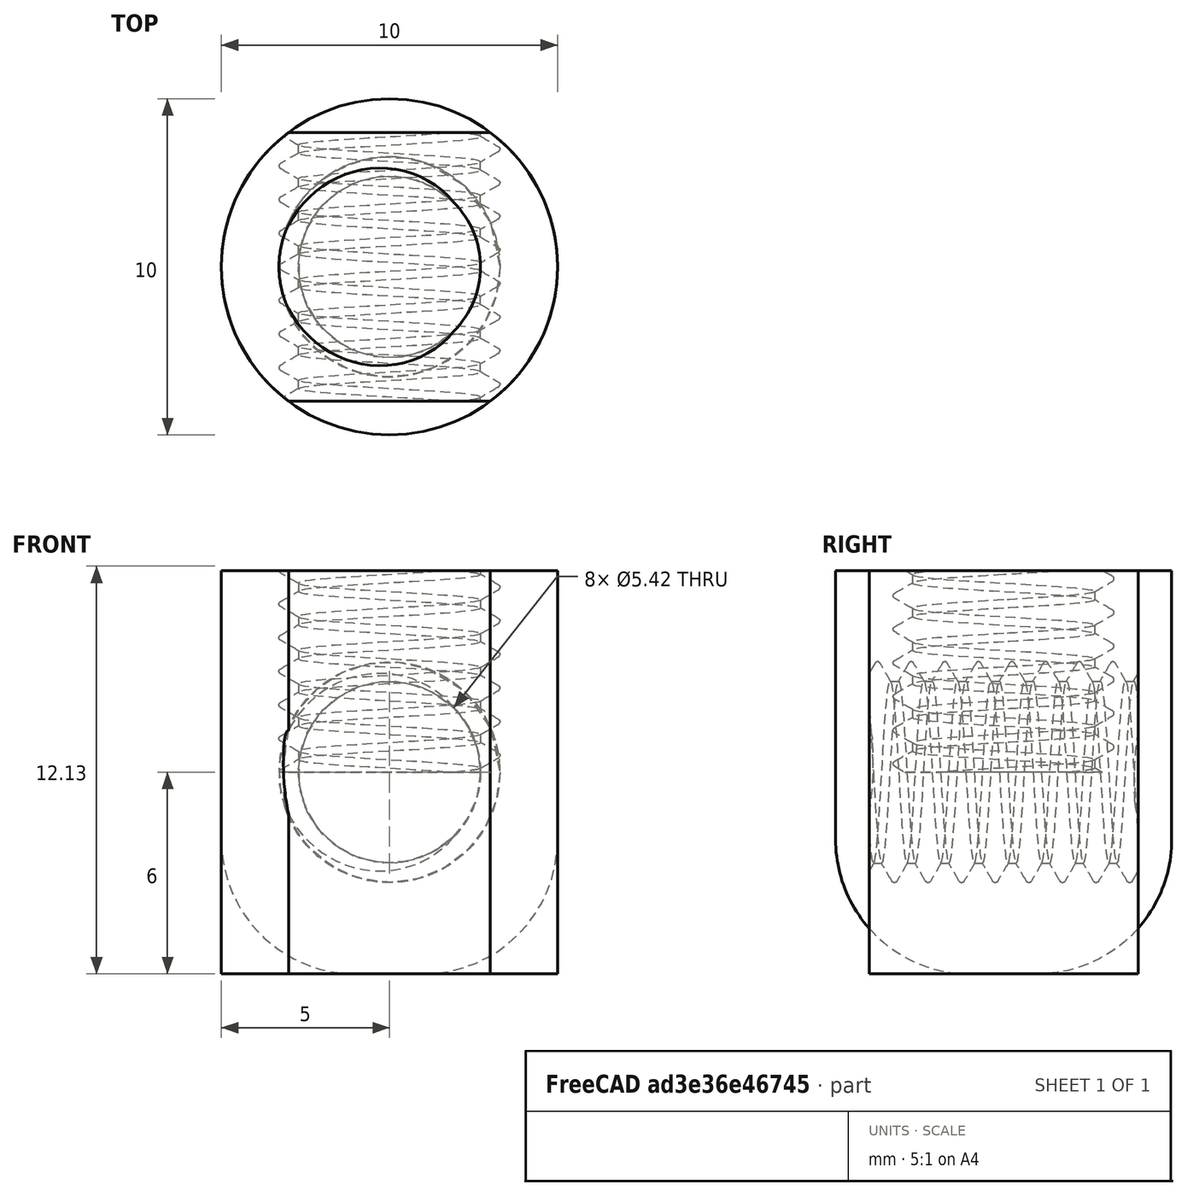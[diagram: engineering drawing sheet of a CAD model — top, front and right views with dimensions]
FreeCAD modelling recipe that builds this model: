
FCSTD DOCUMENT  (FreeCAD 0.21R33771 (Git))
Label: parts
License: All rights reserved
LicenseURL: https://en.wikipedia.org/wiki/All_rights_reserved
objects: Part::Cylinder×2, Part::FeaturePython×2, Part::Cut×2, Part::Box×1, Part::MultiCommon×1, Part::Fillet×1
note: 9 computed .brp shape members not serialized (recipe doc carries the construction recipe); baked Part::Feature solids carry a one-line shape summary decoded from their .brp

FEATURE [Part::Cylinder] Cylinder
  Angle = 360
  AttacherType = Attacher::AttachEngine3D
  FirstAngle = 0
  Height = 12
  Radius = 5
  SecondAngle = 0
FEATURE [Part::Box] Box  label="Cube"
  AttacherType = Attacher::AttachEngine3D
  Height = 12
  Length = 10
  Placement = pos=(-5,-4,0) rot=(0,0,1;0rad)
  Width = 8
FEATURE [Part::MultiCommon] Common
  Shapes = -> [Cylinder,Box]
FEATURE [Part::FeaturePython] ScrewTap  label="6.5x20-ScrewTap001"  # Fasteners workbench fastener (typed FeaturePython)
  Placement = pos=(0,-9,6) rot=(1,0,0;1.5708rad)
  diameter = 29
  diameterCustom = 6.5
  invert = false
  leftHanded = false
  length = 20
  matchOuter = false
  offset = 0
  pitchCustom = 1
  thread = true
  type = 2
FEATURE [Part::Cut] Cut  label="barrelnut_m6_threaded"
  Base = -> Common
  Tool = -> ScrewTap
FEATURE [Part::Cylinder] Cylinder001
  Angle = 360
  AttacherType = Attacher::AttachEngine3D
  FirstAngle = 0
  Height = 12
  Radius = 5
  SecondAngle = 0
FEATURE [Part::FeaturePython] ScrewTap001  label="6.5x20-ScrewTap"  # Fasteners workbench fastener (typed FeaturePython)
  Placement = pos=(0,0,26) rot=(1,0,0;0rad)
  diameter = 29
  diameterCustom = 6.5
  invert = false
  leftHanded = false
  length = 20
  matchOuter = false
  offset = 0
  pitchCustom = 1
  thread = true
  type = 2
FEATURE [Part::Cut] Cut001  label="Cut"
  Base = -> Cylinder001
  Tool = -> ScrewTap001
FEATURE [Part::Fillet] Fillet  label="piston_m6"
  Base = -> Cut001
  Edges = 1 edges r=4: [Edge2]
